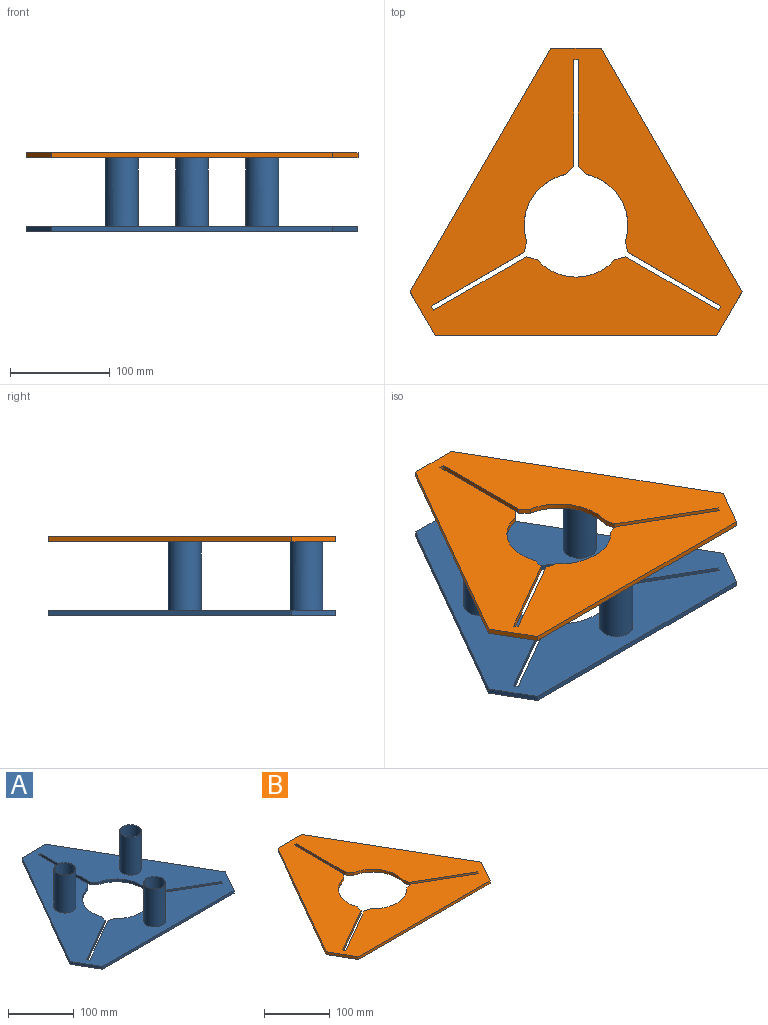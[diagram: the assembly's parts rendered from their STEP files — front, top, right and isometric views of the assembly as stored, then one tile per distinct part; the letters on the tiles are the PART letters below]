
ASSEMBLY  parts=2 mates=2
PART A: 38 faces, bbox 333.4x288.7x75.6 mm
  f0: plane 244.7x141.28mm, normal (0.87,0.5,0), area 1435.4mm2, adj f1,f5,f6,f25
  f1: plane 43.99x25.4mm, normal (0.87,-0.5,0), area 258.1mm2, adj f0,f2,f6,f25
  f2: plane 282.56x5.08mm, normal (0,-1,0), area 1435.4mm2, adj f1,f3,f6,f25
  f3: plane 43.99x25.4mm, normal (-0.87,-0.5,0), area 258.1mm2, adj f2,f4,f6,f25
  f4: plane 244.7x141.28mm, normal (-0.87,0.5,0), area 1435.4mm2, adj f3,f5,f6,f25
  f5: plane 50.8x5.08mm, normal (0,1,0), area 258.1mm2, adj f0,f4,f6,f25
  f6: plane 333.36x288.7mm, normal (0,0,-1), area 50234.1mm2, adj f0,f1,f2,f3,f4,f5,f7,f8
  f7: plane 107.23x5.08mm, normal (-1,0,0), area 544.7mm2, adj f6,f8,f24,f25
  f8: plane 8.08x8.08mm, normal (-0.71,-0.71,0), area 58.1mm2, adj f6,f7,f9,f25
  f9: cylinder r=52.07mm len=67.45mm, axis (0,0,1), area 447mm2, adj f6,f8,f10,f25
  f10: plane 11.04x5.08mm, normal (-0.97,-0.26,0), area 58.1mm2, adj f6,f9,f11,f25
  f11: plane 92.86x53.61mm, normal (-0.5,-0.87,0), area 544.7mm2, adj f6,f10,f12,f25
  f12: plane 5.08x4.12mm, normal (-0.87,0.5,0), area 24.2mm2, adj f6,f11,f13,f25
  f13: plane 92.86x53.61mm, normal (0.5,0.87,0), area 544.7mm2, adj f6,f12,f14,f25
  f14: plane 11.04x5.08mm, normal (-0.26,0.97,0), area 58.1mm2, adj f6,f13,f15,f25
  f15: cylinder r=52.07mm len=77.88mm, axis (0,0,1), area 447mm2, adj f6,f14,f16,f25
  f16: plane 11.04x5.08mm, normal (0.26,0.97,0), area 58.1mm2, adj f6,f15,f17,f25
  f17: plane 92.86x53.61mm, normal (-0.5,0.87,0), area 544.7mm2, adj f6,f16,f18,f25
  f18: plane 5.08x4.12mm, normal (0.87,0.5,0), area 24.2mm2, adj f6,f17,f19,f25
  f19: plane 92.86x53.61mm, normal (0.5,-0.87,0), area 544.7mm2, adj f6,f18,f20,f25
  f20: plane 11.04x5.08mm, normal (0.97,-0.26,0), area 58.1mm2, adj f6,f19,f21,f25
  f21: cylinder r=52.07mm len=67.45mm, axis (0,0,1), area 447mm2, adj f6,f20,f22,f25
  f22: plane 8.08x8.08mm, normal (0.71,-0.71,0), area 58.1mm2, adj f6,f21,f23,f25
  f23: plane 107.23x5.08mm, normal (1,0,0), area 544.7mm2, adj f6,f22,f24,f25
  f24: plane 5.08x4.76mm, normal (0,-1,0), area 24.2mm2, adj f6,f7,f23,f25
  f25: plane 333.36x288.7mm, normal (0,0,1), area 47665.1mm2, adj f0,f1,f2,f3,f4,f5,f7,f8
  f26: cylinder r=16.51mm len=70.49mm, axis (0,0,-1), area 7311.8mm2, adj f25,f28
  f27: cylinder r=16.26mm len=70.49mm, axis (0,0,-1), area 7199.3mm2, adj f28,f29
  f28: plane 33.02x33.02mm, normal (0,0,1), area 26.1mm2, adj f26,f27
  f29: plane 32.51x32.51mm, normal (0,0,1), area 830.2mm2, adj f27
  f30: cylinder r=16.51mm len=70.49mm, axis (0,0,-1), area 7311.8mm2, adj f25,f32
  f31: cylinder r=16.26mm len=70.49mm, axis (0,0,-1), area 7199.3mm2, adj f32,f33
  f32: plane 33.02x33.02mm, normal (0,0,1), area 26.1mm2, adj f30,f31
  f33: plane 32.51x32.51mm, normal (0,0,1), area 830.2mm2, adj f31
  f34: cylinder r=16.51mm len=70.49mm, axis (0,0,-1), area 7311.8mm2, adj f25,f36
  f35: cylinder r=16.26mm len=70.49mm, axis (0,0,-1), area 7199.3mm2, adj f36,f37
  f36: plane 33.02x33.02mm, normal (0,0,1), area 26.1mm2, adj f34,f35
  f37: plane 32.51x32.51mm, normal (0,0,1), area 830.2mm2, adj f35
PART B: 26 faces, bbox 333.4x288.7x5.1 mm
  f0: plane 244.7x141.28mm, normal (0.87,0.5,0), area 1435.4mm2, adj f1,f5,f6,f25
  f1: plane 43.99x25.4mm, normal (0.87,-0.5,0), area 258.1mm2, adj f0,f2,f6,f25
  f2: plane 282.56x5.08mm, normal (0,-1,0), area 1435.4mm2, adj f1,f3,f6,f25
  f3: plane 43.99x25.4mm, normal (-0.87,-0.5,0), area 258.1mm2, adj f2,f4,f6,f25
  f4: plane 244.7x141.28mm, normal (-0.87,0.5,0), area 1435.4mm2, adj f3,f5,f6,f25
  f5: plane 50.8x5.08mm, normal (0,1,0), area 258.1mm2, adj f0,f4,f6,f25
  f6: plane 333.36x288.7mm, normal (0,0,-1), area 50234.1mm2, adj f0,f1,f2,f3,f4,f5,f7,f8
  f7: plane 107.23x5.08mm, normal (-1,0,0), area 544.7mm2, adj f6,f8,f24,f25
  f8: plane 8.08x8.08mm, normal (-0.71,-0.71,0), area 58.1mm2, adj f6,f7,f9,f25
  f9: cylinder r=52.07mm len=67.45mm, axis (0,0,1), area 447mm2, adj f6,f8,f10,f25
  f10: plane 11.04x5.08mm, normal (-0.97,-0.26,0), area 58.1mm2, adj f6,f9,f11,f25
  f11: plane 92.86x53.61mm, normal (-0.5,-0.87,0), area 544.7mm2, adj f6,f10,f12,f25
  f12: plane 5.08x4.12mm, normal (-0.87,0.5,0), area 24.2mm2, adj f6,f11,f13,f25
  f13: plane 92.86x53.61mm, normal (0.5,0.87,0), area 544.7mm2, adj f6,f12,f14,f25
  f14: plane 11.04x5.08mm, normal (-0.26,0.97,0), area 58.1mm2, adj f6,f13,f15,f25
  f15: cylinder r=52.07mm len=77.88mm, axis (0,0,1), area 447mm2, adj f6,f14,f16,f25
  f16: plane 11.04x5.08mm, normal (0.26,0.97,0), area 58.1mm2, adj f6,f15,f17,f25
  f17: plane 92.86x53.61mm, normal (-0.5,0.87,0), area 544.7mm2, adj f6,f16,f18,f25
  f18: plane 5.08x4.12mm, normal (0.87,0.5,0), area 24.2mm2, adj f6,f17,f19,f25
  f19: plane 92.86x53.61mm, normal (0.5,-0.87,0), area 544.7mm2, adj f6,f18,f20,f25
  f20: plane 11.04x5.08mm, normal (0.97,-0.26,0), area 58.1mm2, adj f6,f19,f21,f25
  f21: cylinder r=52.07mm len=67.45mm, axis (0,0,1), area 447mm2, adj f6,f20,f22,f25
  f22: plane 8.08x8.08mm, normal (0.71,-0.71,0), area 58.1mm2, adj f6,f21,f23,f25
  f23: plane 107.23x5.08mm, normal (1,0,0), area 544.7mm2, adj f6,f22,f24,f25
  f24: plane 5.08x4.76mm, normal (0,-1,0), area 24.2mm2, adj f6,f7,f23,f25
  f25: plane 333.36x288.7mm, normal (0,0,1), area 50234.1mm2, adj f0,f1,f2,f3,f4,f5,f7,f8
PLACE A t=(-0.66,-8.74,2.4)mm fixed
PLACE B t=(-0.66,-8.74,76.08)mm
MATE slider B.f9 <-> A.f9  axis (0,0,1) through (-0.66,-8.74,78.62)mm
MATE parallel B.f9 <-> A.f9  axis (0,0,-1) through (-0.66,-8.74,73.54)mm
